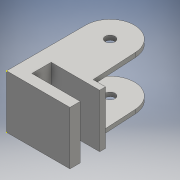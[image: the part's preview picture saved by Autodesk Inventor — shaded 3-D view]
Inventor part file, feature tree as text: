
AUTODESK INVENTOR PART (.ipt)
format: ipt  version: 2016 (Build 200138000, 138)  size: 137,216 bytes
history: native  units: mm
features: sketch x9, extrude x4
ambient origin geometry x8: Origin, YZ Plane, XZ Plane, XY Plane, X Axis, Y Axis, Z Axis, Center Point
bodies: Solid1 (feature_tree)
feature tree (13):
  extrude  "Extrusion1"  Depth=8.0mm
  extrude  "Extrusion2"  Depth=10.0mm
  extrude  "Extrusion3"  Depth=19.989431mm
  sketch  "Sketch4"  dims[d8=22.0mm d9=0.0mm d10=22.0mm d11=0.0mm]
  sketch  "Sketch5"  dims[d12=22.0mm d13=0.0mm]
  sketch  "Sketch6"  dims[d14=28.0mm]
  sketch  "Sketch7"  dims[d15=22.0mm d16=0.0mm]
  sketch  "Sketch8"  dims[d17=18.5mm]
  extrude  "Extrusion4"  Depth=22.0mm TaperAngle=0.0deg
  sketch  "Sketch1"  dims[d0=20.0mm d1=8.0mm]
  sketch  "Sketch2"  dims[d3=4.0mm d4=10.0mm]
  sketch  "Sketch3"  dims[d5=18.0mm d7=19.989431mm]
  sketch  "Sketch9"
